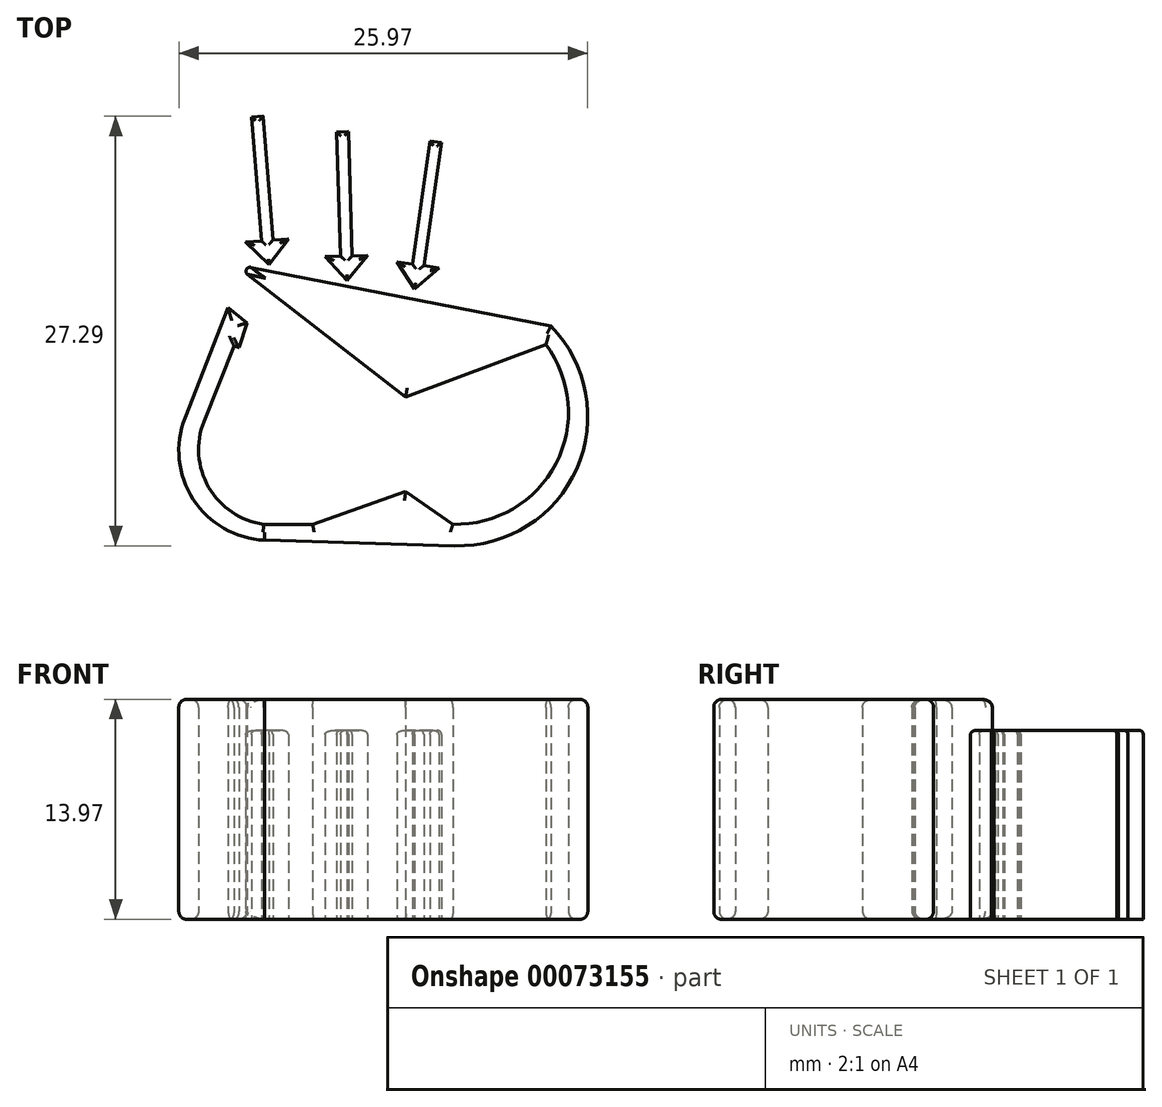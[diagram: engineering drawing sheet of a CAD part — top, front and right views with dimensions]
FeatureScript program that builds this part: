
annotation { "Feature Type Name" : "Feature", "Feature Type Description" : "" }
export const myFeature = defineFeature(function(context is Context, id is Id, definition is map)
    precondition{}
    {
        {
            var Q0;
            Q0=qCreatedBy(makeId("Top.planeOp"),FACE);
            var sketch = newSketch(context, id + "F0", { "sketchPlane" : qUnion([Q0])});
            skLineSegment(sketch, "E0", {"start": v(0, 8.08) * mm, "end": v(8.9, 11.41) * mm});
            skLineSegment(sketch, "E1", {"start": v(-9.02, 0) * mm, "end": v(-5.9, 0) * mm});
            skLineSegment(sketch, "E2", {"start": v(-5.9, 0) * mm, "end": v(0, 2.07) * mm});
            skLineSegment(sketch, "E3", {"start": v(0, 2.07) * mm, "end": v(3, 0) * mm});
            skArc(sketch, "E4", {"start": v(3, 0) * mm, "mid": v(9.54, 3.85) * mm, "end": v(8.9, 11.41) * mm});
            skArc(sketch, "E5", {"start": v(3.1, -1.36) * mm, "mid": v(10.87, 3.55) * mm, "end": v(9.23, 12.6) * mm});
            skLineSegment(sketch, "E6", {"start": v(-14.02, 6.76) * mm, "end": v(-11.27, 13.77) * mm});
            skLineSegment(sketch, "E7", {"start": v(-11.27, 13.77) * mm, "end": v(-10.08, 12.78) * mm});
            skLineSegment(sketch, "E8", {"start": v(-10.08, 12.78) * mm, "end": v(-10.6, 11.22) * mm});
            skLineSegment(sketch, "E9", {"start": v(-10.6, 11.22) * mm, "end": v(-10.9, 11.32) * mm});
            skLineSegment(sketch, "E10", {"start": v(-10.9, 11.32) * mm, "end": v(-12.81, 6.54) * mm});
            skArc(sketch, "E11", {"start": v(-12.81, 6.54) * mm, "mid": v(-12.5, 2.35) * mm, "end": v(-9.02, 0) * mm});
            skArc(sketch, "E12", {"start": v(-14.02, 6.76) * mm, "mid": v(-13.5, 1.58) * mm, "end": v(-8.97, -1) * mm});
            skLineSegment(sketch, "E13", {"start": v(-8.97, -1) * mm, "end": v(3.1, -1.36) * mm});
            skLineSegment(sketch, "E14", {"start": v(9.23, 12.6) * mm, "end": v(-10.88, 16.52) * mm});
            skLineSegment(sketch, "E15", {"start": v(-10.88, 16.52) * mm, "end": v(0, 8.08) * mm});
            skSolve(sketch);
        }
        {
            var Q0;
            Q0=makeQuery(id+"F0.imprint","IMPRINT",FACE,{"disambiguationData":[TD([[makeQuery(id+"F0.imprint","IMPRINT",EDGE,{"derivedFrom":sQuery(id+"F0.wireOp",EDGE,"E0")}),1.0]])]});
            extrude(context, id + "F1", {"entities" : qUnion([Q0]), "depth" : 13.97 * mm});
        }
        {
            var Q0;
            Q0=qCreatedBy(makeId("Top.planeOp"),FACE);
            var sketch = newSketch(context, id + "F2", { "sketchPlane" : qUnion([Q0])});
            skLineSegment(sketch, "E16", {"start": v(-8.68, 16.48) * mm, "end": v(-7.45, 18.13) * mm});
            skLineSegment(sketch, "E17", {"start": v(-7.45, 18.13) * mm, "end": v(-8.44, 18.05) * mm});
            skLineSegment(sketch, "E18", {"start": v(-8.44, 18.05) * mm, "end": v(-9.06, 25.92) * mm});
            skLineSegment(sketch, "E19.MirrorCS", {"start": v(-9.17, 18) * mm, "end": v(-9.8, 25.86) * mm});
            skLineSegment(sketch, "E20.MirrorCS", {"start": v(-10.16, 17.92) * mm, "end": v(-9.17, 18) * mm});
            skLineSegment(sketch, "E21.MirrorCS", {"start": v(-8.68, 16.48) * mm, "end": v(-10.16, 17.92) * mm});
            skLineSegment(sketch, "E22", {"start": v(-9.8, 25.86) * mm, "end": v(-9.06, 25.92) * mm});
            skLineSegment(sketch, "E23", {"start": v(-3.72, 15.5) * mm, "end": v(-2.4, 17.08) * mm});
            skLineSegment(sketch, "E24", {"start": v(-2.4, 17.08) * mm, "end": v(-3.4, 17.05) * mm});
            skLineSegment(sketch, "E25", {"start": v(-3.4, 17.05) * mm, "end": v(-3.65, 24.94) * mm});
            skLineSegment(sketch, "E26.MirrorCS", {"start": v(-4.13, 17.03) * mm, "end": v(-4.38, 24.91) * mm});
            skLineSegment(sketch, "E27.MirrorCS", {"start": v(-5.12, 17) * mm, "end": v(-4.13, 17.03) * mm});
            skLineSegment(sketch, "E28.MirrorCS", {"start": v(-3.72, 15.5) * mm, "end": v(-5.12, 17) * mm});
            skLineSegment(sketch, "E29", {"start": v(-4.38, 24.91) * mm, "end": v(-3.65, 24.94) * mm});
            skLineSegment(sketch, "E30", {"start": v(0.56, 14.95) * mm, "end": v(2.13, 16.28) * mm});
            skLineSegment(sketch, "E31", {"start": v(2.13, 16.28) * mm, "end": v(1.15, 16.43) * mm});
            skLineSegment(sketch, "E32", {"start": v(1.15, 16.43) * mm, "end": v(2.27, 24.23) * mm});
            skLineSegment(sketch, "E33.MirrorCS", {"start": v(0.42, 16.53) * mm, "end": v(1.55, 24.34) * mm});
            skLineSegment(sketch, "E34.MirrorCS", {"start": v(-0.56, 16.67) * mm, "end": v(0.42, 16.53) * mm});
            skLineSegment(sketch, "E35.MirrorCS", {"start": v(0.56, 14.95) * mm, "end": v(-0.56, 16.67) * mm});
            skLineSegment(sketch, "E36", {"start": v(1.55, 24.34) * mm, "end": v(2.27, 24.23) * mm});
            skSolve(sketch);
        }
        {
            var Q0;
            Q0 = qSketchRegion(id + "F2", true);
            extrude(context, id + "F3", {"entities" : qUnion([Q0]), "depth" : 12 * mm});
        }
        {
            var Q0;
            Q0=makeQuery(id+"F1.opExtrude","CAP_FACE",FACE,{"disambiguationData":[OSD([sQuery(id+"F0.wireOp",EDGE,"9T2jLX1K-ABNv-7rBE-ews3-E361xKiuboZv"),sQuery(id+"F0.wireOp",EDGE,"E0"),sQuery(id+"F0.wireOp",EDGE,"5hrsAgLx-odRK-C1TO-J7ZC-rabmQv0Jw3fn"),sQuery(id+"F0.wireOp",EDGE,"E1"),sQuery(id+"F0.wireOp",EDGE,"E2"),sQuery(id+"F0.wireOp",EDGE,"E3"),sQuery(id+"F0.wireOp",EDGE,"E4"),sQuery(id+"F0.wireOp",EDGE,"E5"),sQuery(id+"F0.wireOp",EDGE,"E6"),sQuery(id+"F0.wireOp",EDGE,"E7"),sQuery(id+"F0.wireOp",EDGE,"E8"),sQuery(id+"F0.wireOp",EDGE,"E9"),sQuery(id+"F0.wireOp",EDGE,"E10"),sQuery(id+"F0.wireOp",EDGE,"E11"),sQuery(id+"F0.wireOp",EDGE,"E12"),sQuery(id+"F0.wireOp",EDGE,"E13")])],"isStart":false});
            var Q1;
            Q1=makeQuery(id+"F1.opExtrude","CAP_FACE",FACE,{"disambiguationData":[OSD([sQuery(id+"F0.wireOp",EDGE,"9T2jLX1K-ABNv-7rBE-ews3-E361xKiuboZv"),sQuery(id+"F0.wireOp",EDGE,"E0"),sQuery(id+"F0.wireOp",EDGE,"5hrsAgLx-odRK-C1TO-J7ZC-rabmQv0Jw3fn"),sQuery(id+"F0.wireOp",EDGE,"E1"),sQuery(id+"F0.wireOp",EDGE,"E2"),sQuery(id+"F0.wireOp",EDGE,"E3"),sQuery(id+"F0.wireOp",EDGE,"E4"),sQuery(id+"F0.wireOp",EDGE,"E5"),sQuery(id+"F0.wireOp",EDGE,"E6"),sQuery(id+"F0.wireOp",EDGE,"E7"),sQuery(id+"F0.wireOp",EDGE,"E8"),sQuery(id+"F0.wireOp",EDGE,"E9"),sQuery(id+"F0.wireOp",EDGE,"E10"),sQuery(id+"F0.wireOp",EDGE,"E11"),sQuery(id+"F0.wireOp",EDGE,"E12"),sQuery(id+"F0.wireOp",EDGE,"E13")])],"isStart":true});
            fillet(context, id + "F4", {"entities" : qUnion([Q0, Q1]), "radius" : .5 * mm, "tangentPropagation" : true, "allowEdgeOverflow" : false});
        }
        {
            var Q0;
            Q0=makeQuery(id+"F1.opExtrude","SWEPT_EDGE",EDGE,{"disambiguationData":[OSD([sQuery(id+"F0.wireOp",EDGE,"E14"),sQuery(id+"F0.wireOp",EDGE,"E15")])]});
            var Q1;
            Q1=makeQuery(id+"F3.opExtrude","CAP_FACE",FACE,{"disambiguationData":[OSD([sQuery(id+"F2.wireOp",EDGE,"E16"),sQuery(id+"F2.wireOp",EDGE,"E17"),sQuery(id+"F2.wireOp",EDGE,"E18"),sQuery(id+"F2.wireOp",EDGE,"E19.MirrorCS"),sQuery(id+"F2.wireOp",EDGE,"E20.MirrorCS"),sQuery(id+"F2.wireOp",EDGE,"E21.MirrorCS"),sQuery(id+"F2.wireOp",EDGE,"E22")])],"isStart":false});
            var Q2;
            Q2=makeQuery(id+"F3.opExtrude","CAP_FACE",FACE,{"disambiguationData":[OSD([sQuery(id+"F2.wireOp",EDGE,"E23"),sQuery(id+"F2.wireOp",EDGE,"E24"),sQuery(id+"F2.wireOp",EDGE,"E25"),sQuery(id+"F2.wireOp",EDGE,"E26.MirrorCS"),sQuery(id+"F2.wireOp",EDGE,"E27.MirrorCS"),sQuery(id+"F2.wireOp",EDGE,"E28.MirrorCS"),sQuery(id+"F2.wireOp",EDGE,"E29")])],"isStart":false});
            var Q3;
            Q3=makeQuery(id+"F3.opExtrude","CAP_FACE",FACE,{"disambiguationData":[OSD([sQuery(id+"F2.wireOp",EDGE,"E30"),sQuery(id+"F2.wireOp",EDGE,"E31"),sQuery(id+"F2.wireOp",EDGE,"E32"),sQuery(id+"F2.wireOp",EDGE,"E33.MirrorCS"),sQuery(id+"F2.wireOp",EDGE,"E34.MirrorCS"),sQuery(id+"F2.wireOp",EDGE,"E35.MirrorCS"),sQuery(id+"F2.wireOp",EDGE,"E36")])],"isStart":false});
            fillet(context, id + "F5", {"entities" : qUnion([Q0, Q1, Q2, Q3]), "radius" : .25 * mm, "tangentPropagation" : true, "allowEdgeOverflow" : false});
        }
    });
